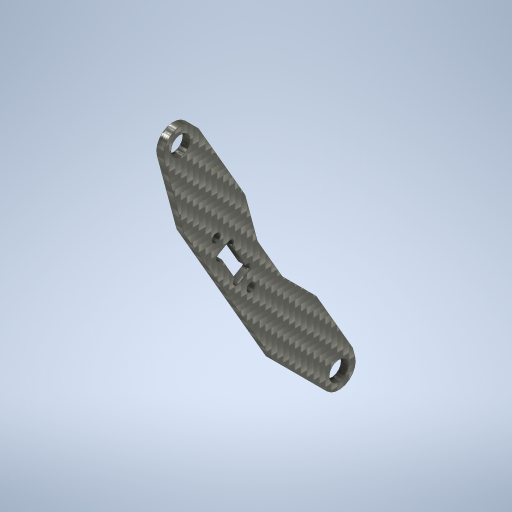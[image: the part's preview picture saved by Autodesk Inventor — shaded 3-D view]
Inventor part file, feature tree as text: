
AUTODESK INVENTOR PART (.ipt)
format: ipt  version: 2024.2 (Build 282272000, 272)  size: 356,864 bytes
history: native  units: mm
features: hole x2, other x1, extrude x1, sketch x1
ambient origin geometry x8: Origin, YZ Plane, XZ Plane, XY Plane, X Axis, Y Axis, Z Axis, Center Point
bodies: Solid1 (feature_tree)
feature tree (5):
  other  "LegLinkBasis.ipt"
  extrude  "Extrusion1"  Depth=3.0mm TaperAngle=0.0deg
  hole  "Phi8.0-H7"  [1 undecoded]
  hole  "Phi3.5"  [1 undecoded]
  sketch  "Sketch1"  dims[d0=10.0mm d1=3.0mm d2=0.0mm d3=8.0mm d4=6.0mm d5=4.0mm d6=2.0mm d7=90.0deg d8=8.0mm d9=20.594885mm d10=3.5mm d11=6.0mm d12=4.0mm d13=2.0mm d14=90.0deg d15=8.0mm d16=20.594885mm d17=2.0mm]
note: 2 required parameter values undecoded (feature->parameter linkage not recoverable at this tier; creation-order binding heuristic only, values carry confidence <= 0.55)
